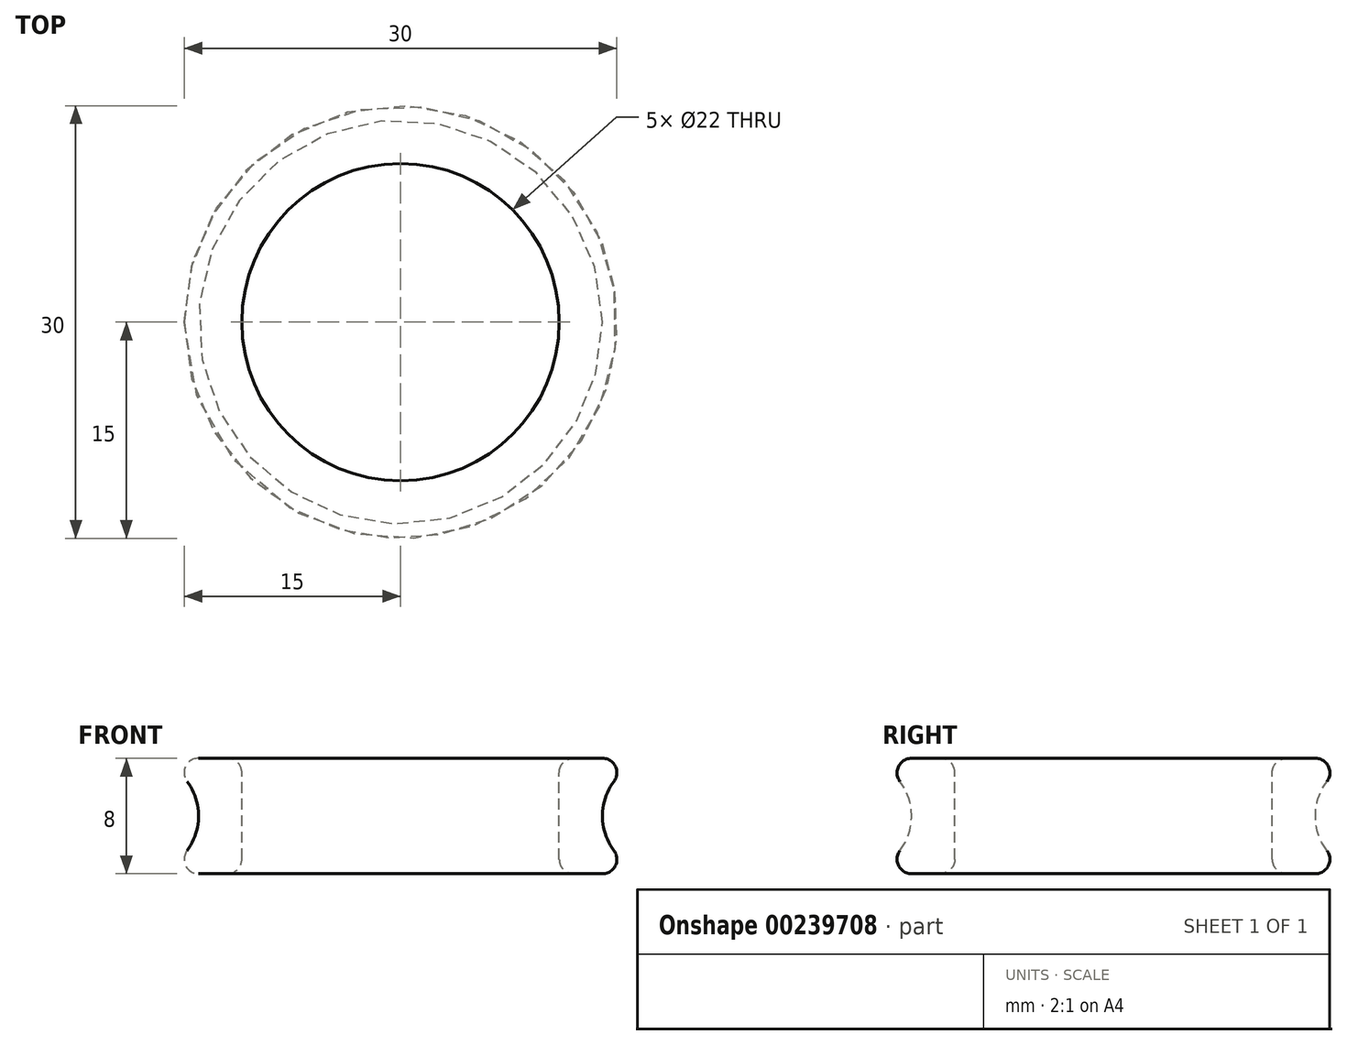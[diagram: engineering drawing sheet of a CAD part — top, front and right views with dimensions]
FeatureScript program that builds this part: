
annotation { "Feature Type Name" : "Feature", "Feature Type Description" : "" }
export const myFeature = defineFeature(function(context is Context, id is Id, definition is map)
    precondition{}
    {
        {
            var Q0;
            Q0=qCreatedBy(makeId("Front.planeOp"),FACE);
            var sketch = newSketch(context, id + "F0", { "sketchPlane" : qUnion([Q0])});
            skLineSegment(sketch, "E0", {"start": v(0, 75.93) * mm, "end": v(0, -83.29) * mm, "construction": true});
            skLineSegment(sketch, "E1.bottom", {"start": v(-15, 4) * mm, "end": v(-11, 4) * mm});
            skLineSegment(sketch, "E1.top", {"start": v(-15, -4) * mm, "end": v(-11, -4) * mm});
            skLineSegment(sketch, "E1.left", {"start": v(-15, 4) * mm, "end": v(-15, 2.65) * mm});
            skLineSegment(sketch, "E1.right", {"start": v(-11, 4) * mm, "end": v(-11, 0) * mm});
            skArc(sketch, "E2", {"start": v(-15, -2.65) * mm, "mid": v(-14, 0) * mm, "end": v(-15, 2.65) * mm});
            skLineSegment(sketch, "E3", {"start": v(-15, -2.65) * mm, "end": v(-15, -4) * mm});
            skLineSegment(sketch, "E4", {"start": v(-11, 0) * mm, "end": v(-11, -4) * mm});
            skSolve(sketch);
        }
        {
            var Q0;
            Q0 = qSketchRegion(id + "F0", true);
            var Q1;
            Q1=sQuery(id+"F0.wireOp",EDGE,"E0");
            revolve(context, id + "F1", {"entities" : qUnion([Q0]), "axis" : qUnion([Q1]), "revolveType" : RevolveType.FULL});
        }
        {
            var Q0;
            Q0=makeQuery(id+"F1.opRevolve","SWEPT_EDGE",EDGE,{"disambiguationData":[OSD([sQuery(id+"F0.wireOp",EDGE,"E1.left"),sQuery(id+"F0.wireOp",EDGE,"E2")])]});
            var Q1;
            Q1=makeQuery(id+"F1.opRevolve","SWEPT_EDGE",EDGE,{"disambiguationData":[OSD([sQuery(id+"F0.wireOp",EDGE,"E1.bottom"),sQuery(id+"F0.wireOp",EDGE,"E1.left")])]});
            var Q2;
            Q2=makeQuery(id+"F1.opRevolve","SWEPT_EDGE",EDGE,{"disambiguationData":[OSD([sQuery(id+"F0.wireOp",EDGE,"E1.bottom"),sQuery(id+"F0.wireOp",EDGE,"E1.right")])]});
            var Q3;
            Q3=makeQuery(id+"F1.opRevolve","SWEPT_EDGE",EDGE,{"disambiguationData":[OSD([sQuery(id+"F0.wireOp",EDGE,"E1.top"),sQuery(id+"F0.wireOp",EDGE,"E4")])]});
            var Q4;
            Q4=makeQuery(id+"F1.opRevolve","SWEPT_EDGE",EDGE,{"disambiguationData":[OSD([sQuery(id+"F0.wireOp",EDGE,"E2"),sQuery(id+"F0.wireOp",EDGE,"E3")])]});
            var Q5;
            Q5=makeQuery(id+"F1.opRevolve","SWEPT_EDGE",EDGE,{"disambiguationData":[OSD([sQuery(id+"F0.wireOp",EDGE,"E1.top"),sQuery(id+"F0.wireOp",EDGE,"E3")])]});
            fillet(context, id + "F2", {"entities" : qUnion([Q0, Q1, Q2, Q3, Q4, Q5]), "radius" : 1 * mm, "tangentPropagation" : true, "allowEdgeOverflow" : false});
        }
    });
